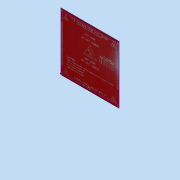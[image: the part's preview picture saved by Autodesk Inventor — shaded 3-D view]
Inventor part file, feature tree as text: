
AUTODESK INVENTOR PART (.ipt)
format: ipt  version: 2015 (Build 190159000, 159)  size: 126,976 bytes
history: native  units: in
note: dims shown in document units (in); Inventor stores cm internally (conversion verified against a paired STEP export)
features: sketch x3, extrude x1, hole x1, other x1
ambient origin geometry x8: Origin, YZ Plane, XZ Plane, XY Plane, X Axis, Y Axis, Z Axis, Center Point
bodies: Solid1 (feature_tree)
feature tree (6):
  extrude  "Extrusion1"  Depth=8.4252in
  sketch  "Sketch4"  dims[d4=0.065in d5=0.0in d41=0.1181in]
  hole  "Hole1"  [1 undecoded]
  sketch  "Sketch3"  dims[d2=8.4252in d3=8.4252in]
  other  "Image2"
  sketch  "Sketch5"  dims[d42=0.1181in d43=0.1181in d44=0.1181in d45=0.1181in d46=0.1181in d47=0.1181in d48=0.1181in d49=0.1181in d50=0.75in d51=0.375in d52=0.25in d53=0.5635in d54=1.0in d55=0.8108in]
note: 1 required parameter value undecoded (feature->parameter linkage not recoverable at this tier; creation-order binding heuristic only, values carry confidence <= 0.55)
